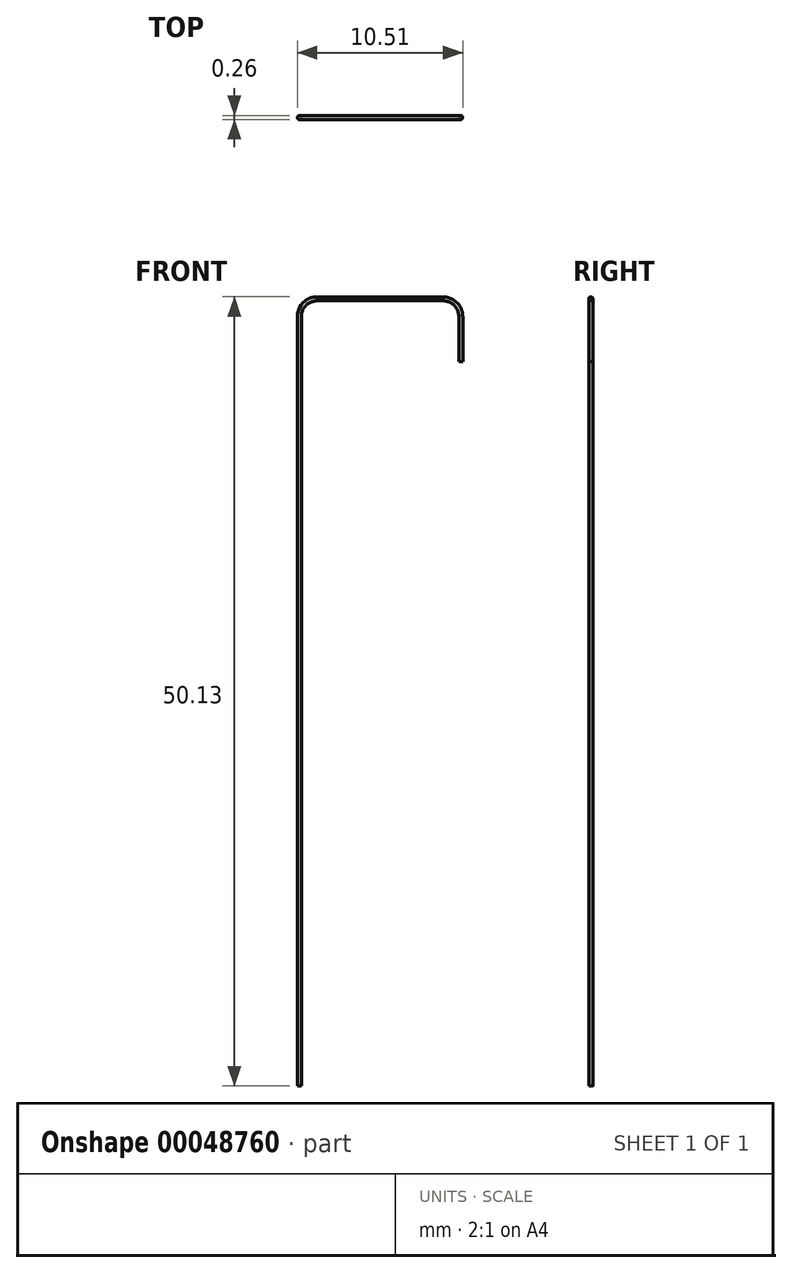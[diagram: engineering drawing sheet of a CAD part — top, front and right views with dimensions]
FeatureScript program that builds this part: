
annotation { "Feature Type Name" : "Feature", "Feature Type Description" : "" }
export const myFeature = defineFeature(function(context is Context, id is Id, definition is map)
    precondition{}
    {
        {
            var Q0;
            Q0=qCreatedBy(makeId("Top.planeOp"),FACE);
            var sketch = newSketch(context, id + "F0", { "sketchPlane" : qUnion([Q0])});
            skCircle(sketch, "E0", {"center": v(0, 0) * mm, "radius": 0.13 * mm});
            skSolve(sketch);
        }
        {
            var Q0;
            Q0=qCreatedBy(makeId("Front.planeOp"),FACE);
            var sketch = newSketch(context, id + "F1", { "sketchPlane" : qUnion([Q0])});
            skLineSegment(sketch, "E1", {"start": v(0, 0) * mm, "end": v(0, 48.88) * mm});
            skLineSegment(sketch, "E2", {"start": v(1.13, 50) * mm, "end": v(9.13, 50) * mm});
            skLineSegment(sketch, "E3", {"start": v(10.25, 48.88) * mm, "end": v(10.25, 46) * mm});
            skPoint(sketch, "E4.visualSharp", {"position": v(0, 50) * mm});
            skArc(sketch, "E4.filletArc", {"start": v(1.13, 50) * mm, "mid": v(0.33, 49.67) * mm, "end": v(0, 48.88) * mm});
            skPoint(sketch, "E5.visualSharp", {"position": v(10.25, 50) * mm});
            skArc(sketch, "E5.filletArc", {"start": v(10.25, 48.88) * mm, "mid": v(9.92, 49.67) * mm, "end": v(9.13, 50) * mm});
            skSolve(sketch);
        }
        {
            var Q0;
            Q0=makeQuery(id+"F0.imprint","IMPRINT",FACE,{"disambiguationData":[TD([[makeQuery(id+"F0.imprint","IMPRINT",EDGE,{"derivedFrom":sQuery(id+"F0.wireOp",EDGE,"E0")}),1.0]])]});
            var Q1;
            Q1=sQuery(id+"F1.wireOp",EDGE,"E1");
            var Q2;
            Q2=sQuery(id+"F1.wireOp",EDGE,"E4.filletArc");
            var Q3;
            Q3=sQuery(id+"F1.wireOp",EDGE,"E2");
            var Q4;
            Q4=sQuery(id+"F1.wireOp",EDGE,"E5.filletArc");
            var Q5;
            Q5=sQuery(id+"F1.wireOp",EDGE,"E3");
            sweep(context, id + "F2", {"profiles" : qUnion([Q0]), "path" : qUnion([Q1, Q2, Q3, Q4, Q5])});
        }
    });
